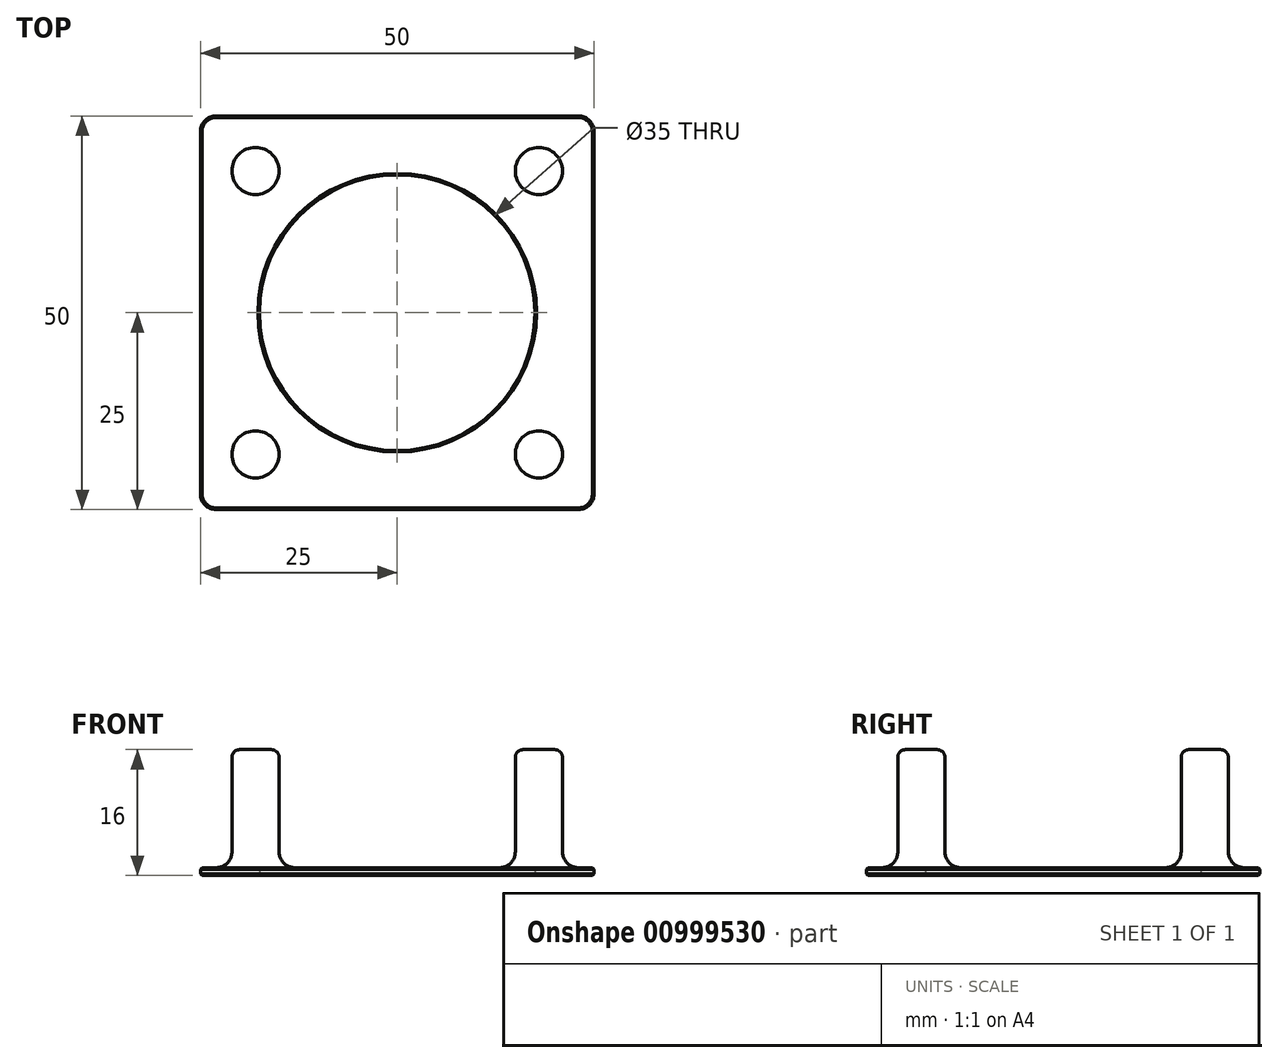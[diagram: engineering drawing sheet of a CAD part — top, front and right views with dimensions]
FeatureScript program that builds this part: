
annotation { "Feature Type Name" : "Feature", "Feature Type Description" : "" }
export const myFeature = defineFeature(function(context is Context, id is Id, definition is map)
    precondition{}
    {
        {
            var Q0;
            Q0=qCreatedBy(makeId("Top.planeOp"),FACE);
            var sketch = newSketch(context, id + "F0", { "sketchPlane" : qUnion([Q0])});
            skLineSegment(sketch, "E0.bottom", {"start": v(25, 25) * mm, "end": v(-25, 25) * mm});
            skLineSegment(sketch, "E0.top", {"start": v(25, -25) * mm, "end": v(-25, -25) * mm});
            skLineSegment(sketch, "E0.left", {"start": v(25, 25) * mm, "end": v(25, -25) * mm});
            skLineSegment(sketch, "E0.right", {"start": v(-25, 25) * mm, "end": v(-25, -25) * mm});
            skPoint(sketch, "E0.middle", {"position": v(0, 0) * mm});
            skCircle(sketch, "E1", {"center": v(0, 0) * mm, "radius": 17.5 * mm});
            skCircle(sketch, "E2", {"center": v(-18, 18) * mm, "radius": 3 * mm});
            skCircle(sketch, "E3.0.1.0", {"center": v(-18, -18) * mm, "radius": 3 * mm});
            skCircle(sketch, "E3.1.0.0", {"center": v(18, 18) * mm, "radius": 3 * mm});
            skCircle(sketch, "E3.1.1.0", {"center": v(18, -18) * mm, "radius": 3 * mm});
            skLineSegment(sketch, "E3.direction1", {"start": v(-18, 18) * mm, "end": v(18, 18) * mm, "construction": true});
            skLineSegment(sketch, "E3.direction2", {"start": v(-18, 18) * mm, "end": v(-18, -18) * mm, "construction": true});
            skSolve(sketch);
        }
        {
            var Q0;
            Q0=makeQuery(id+"F0.imprint","IMPRINT",FACE,{"disambiguationData":[TD([[makeQuery(id+"F0.imprint","IMPRINT",EDGE,{"derivedFrom":sQuery(id+"F0.wireOp",EDGE,"E2")}),1.0]])]});
            var Q1;
            Q1=makeQuery(id+"F0.imprint","IMPRINT",FACE,{"disambiguationData":[TD([[makeQuery(id+"F0.imprint","IMPRINT",EDGE,{"derivedFrom":sQuery(id+"F0.wireOp",EDGE,"E3.0.1.0")}),1.0]])]});
            var Q2;
            Q2=makeQuery(id+"F0.imprint","IMPRINT",FACE,{"disambiguationData":[TD([[makeQuery(id+"F0.imprint","IMPRINT",EDGE,{"derivedFrom":sQuery(id+"F0.wireOp",EDGE,"E3.1.1.0")}),1.0]])]});
            var Q3;
            Q3=makeQuery(id+"F0.imprint","IMPRINT",FACE,{"disambiguationData":[TD([[makeQuery(id+"F0.imprint","IMPRINT",EDGE,{"derivedFrom":sQuery(id+"F0.wireOp",EDGE,"E3.1.0.0")}),1.0]])]});
            var Q4;
            Q4=makeQuery(id+"F0.imprint","IMPRINT",FACE,{"disambiguationData":[TD([[makeQuery(id+"F0.imprint","IMPRINT",EDGE,{"derivedFrom":sQuery(id+"F0.wireOp",EDGE,"E0.bottom")}),1.0]])]});
            extrude(context, id + "F1", {"entities" : qUnion([Q0, Q1, Q2, Q3, Q4]), "depth" : 1 * mm, "offsetDistance" : 25 * mm});
        }
        {
            var Q0;
            Q0=makeQuery(id+"F1.opExtrude","SWEPT_EDGE",EDGE,{"disambiguationData":[OSD([sQuery(id+"F0.wireOp",EDGE,"E0.top"),sQuery(id+"F0.wireOp",EDGE,"E0.right")])]});
            var Q1;
            Q1=makeQuery(id+"F1.opExtrude","SWEPT_EDGE",EDGE,{"disambiguationData":[OSD([sQuery(id+"F0.wireOp",EDGE,"E0.top"),sQuery(id+"F0.wireOp",EDGE,"E0.left")])]});
            var Q2;
            Q2=makeQuery(id+"F1.opExtrude","SWEPT_EDGE",EDGE,{"disambiguationData":[OSD([sQuery(id+"F0.wireOp",EDGE,"E0.bottom"),sQuery(id+"F0.wireOp",EDGE,"E0.left")])]});
            var Q3;
            Q3=makeQuery(id+"F1.opExtrude","SWEPT_EDGE",EDGE,{"disambiguationData":[OSD([sQuery(id+"F0.wireOp",EDGE,"E0.bottom"),sQuery(id+"F0.wireOp",EDGE,"E0.right")])]});
            fillet(context, id + "F2", {"entities" : qUnion([Q0, Q1, Q2, Q3]), "radius" : 2 * mm, "tangentPropagation" : true, "allowEdgeOverflow" : false});
        }
        {
            var Q0;
            Q0=makeQuery(id+"F0.imprint","IMPRINT",FACE,{"disambiguationData":[TD([[makeQuery(id+"F0.imprint","IMPRINT",EDGE,{"derivedFrom":sQuery(id+"F0.wireOp",EDGE,"E3.0.1.0")}),1.0]])]});
            var Q1;
            Q1=makeQuery(id+"F0.imprint","IMPRINT",FACE,{"disambiguationData":[TD([[makeQuery(id+"F0.imprint","IMPRINT",EDGE,{"derivedFrom":sQuery(id+"F0.wireOp",EDGE,"E2")}),1.0]])]});
            var Q2;
            Q2=makeQuery(id+"F0.imprint","IMPRINT",FACE,{"disambiguationData":[TD([[makeQuery(id+"F0.imprint","IMPRINT",EDGE,{"derivedFrom":sQuery(id+"F0.wireOp",EDGE,"E3.1.0.0")}),1.0]])]});
            var Q3;
            Q3=makeQuery(id+"F0.imprint","IMPRINT",FACE,{"disambiguationData":[TD([[makeQuery(id+"F0.imprint","IMPRINT",EDGE,{"derivedFrom":sQuery(id+"F0.wireOp",EDGE,"E3.1.1.0")}),1.0]])]});
            extrude(context, id + "F3", {"entities" : qUnion([Q0, Q1, Q2, Q3]), "operationType" : NewBodyOperationType.ADD, "depth" : (1 + 15) * mm, "offsetDistance" : 25 * mm});
        }
        {
            var Q0;
            Q0=makeQuery(id+"F1.opExtrude","CAP_FACE",FACE,{"disambiguationData":[OSD([sQuery(id+"F0.wireOp",EDGE,"E0.bottom"),sQuery(id+"F0.wireOp",EDGE,"E0.top"),sQuery(id+"F0.wireOp",EDGE,"E0.left"),sQuery(id+"F0.wireOp",EDGE,"E0.right"),sQuery(id+"F0.wireOp",EDGE,"E1")])],"isStart":true});
            var Q1;
            Q1=makeQuery(id+"F1.opExtrude","CAP_EDGE",EDGE,{"disambiguationData":[OSD([sQuery(id+"F0.wireOp",EDGE,"E1")])],"isStart":false});
            var Q2;
            Q2=makeQuery(id+"F1.opExtrude","CAP_EDGE",EDGE,{"disambiguationData":[OSD([sQuery(id+"F0.wireOp",EDGE,"E0.left")])],"isStart":false});
            chamfer(context, id + "F4", {"entities" : qUnion([Q0, Q1, Q2]), "width" : 0.2 * mm, "tangentPropagation" : true});
        }
        {
            var Q0;
            Q0=makeQuery(id+"F3.opExtrude","CAP_FACE",FACE,{"disambiguationData":[OSD([sQuery(id+"F0.wireOp",EDGE,"E3.1.1.0")])],"isStart":false});
            var Q1;
            Q1=makeQuery(id+"F3.opExtrude","CAP_FACE",FACE,{"disambiguationData":[OSD([sQuery(id+"F0.wireOp",EDGE,"E3.0.1.0")])],"isStart":false});
            var Q2;
            Q2=makeQuery(id+"F3.opExtrude","CAP_FACE",FACE,{"disambiguationData":[OSD([sQuery(id+"F0.wireOp",EDGE,"E2")])],"isStart":false});
            var Q3;
            Q3=makeQuery(id+"F3.opExtrude","CAP_FACE",FACE,{"disambiguationData":[OSD([sQuery(id+"F0.wireOp",EDGE,"E3.1.0.0")])],"isStart":false});
            fillet(context, id + "F5", {"entities" : qUnion([Q0, Q1, Q2, Q3]), "radius" : 1 * mm, "tangentPropagation" : true, "allowEdgeOverflow" : false});
        }
        {
            var Q0;
            Q0=makeQuery(id+"F3.boolean.opBoolean","INTERSECT",EDGE,{"derivedFrom":[makeQuery(id+"F1.opExtrude","CAP_FACE",FACE,{"disambiguationData":[OSD([sQuery(id+"F0.wireOp",EDGE,"E0.bottom"),sQuery(id+"F0.wireOp",EDGE,"E0.top"),sQuery(id+"F0.wireOp",EDGE,"E0.left"),sQuery(id+"F0.wireOp",EDGE,"E0.right"),sQuery(id+"F0.wireOp",EDGE,"E1")])],"isStart":false}),makeQuery(id+"F3.opExtrude","SWEPT_FACE",FACE,{"disambiguationData":[OSD([sQuery(id+"F0.wireOp",EDGE,"E3.0.1.0")])]})]});
            var Q1;
            Q1=makeQuery(id+"F3.boolean.opBoolean","INTERSECT",EDGE,{"derivedFrom":[makeQuery(id+"F1.opExtrude","CAP_FACE",FACE,{"disambiguationData":[OSD([sQuery(id+"F0.wireOp",EDGE,"E0.bottom"),sQuery(id+"F0.wireOp",EDGE,"E0.top"),sQuery(id+"F0.wireOp",EDGE,"E0.left"),sQuery(id+"F0.wireOp",EDGE,"E0.right"),sQuery(id+"F0.wireOp",EDGE,"E1")])],"isStart":false}),makeQuery(id+"F3.opExtrude","SWEPT_FACE",FACE,{"disambiguationData":[OSD([sQuery(id+"F0.wireOp",EDGE,"E3.1.1.0")])]})]});
            var Q2;
            Q2=makeQuery(id+"F3.boolean.opBoolean","INTERSECT",EDGE,{"derivedFrom":[makeQuery(id+"F1.opExtrude","CAP_FACE",FACE,{"disambiguationData":[OSD([sQuery(id+"F0.wireOp",EDGE,"E0.bottom"),sQuery(id+"F0.wireOp",EDGE,"E0.top"),sQuery(id+"F0.wireOp",EDGE,"E0.left"),sQuery(id+"F0.wireOp",EDGE,"E0.right"),sQuery(id+"F0.wireOp",EDGE,"E1")])],"isStart":false}),makeQuery(id+"F3.opExtrude","SWEPT_FACE",FACE,{"disambiguationData":[OSD([sQuery(id+"F0.wireOp",EDGE,"E2")])]})]});
            var Q3;
            Q3=makeQuery(id+"F3.boolean.opBoolean","INTERSECT",EDGE,{"derivedFrom":[makeQuery(id+"F1.opExtrude","CAP_FACE",FACE,{"disambiguationData":[OSD([sQuery(id+"F0.wireOp",EDGE,"E0.bottom"),sQuery(id+"F0.wireOp",EDGE,"E0.top"),sQuery(id+"F0.wireOp",EDGE,"E0.left"),sQuery(id+"F0.wireOp",EDGE,"E0.right"),sQuery(id+"F0.wireOp",EDGE,"E1")])],"isStart":false}),makeQuery(id+"F3.opExtrude","SWEPT_FACE",FACE,{"disambiguationData":[OSD([sQuery(id+"F0.wireOp",EDGE,"E3.1.0.0")])]})]});
            fillet(context, id + "F6", {"entities" : qUnion([Q0, Q1, Q2, Q3]), "radius" : 2 * mm, "tangentPropagation" : true, "allowEdgeOverflow" : false});
        }
    });
